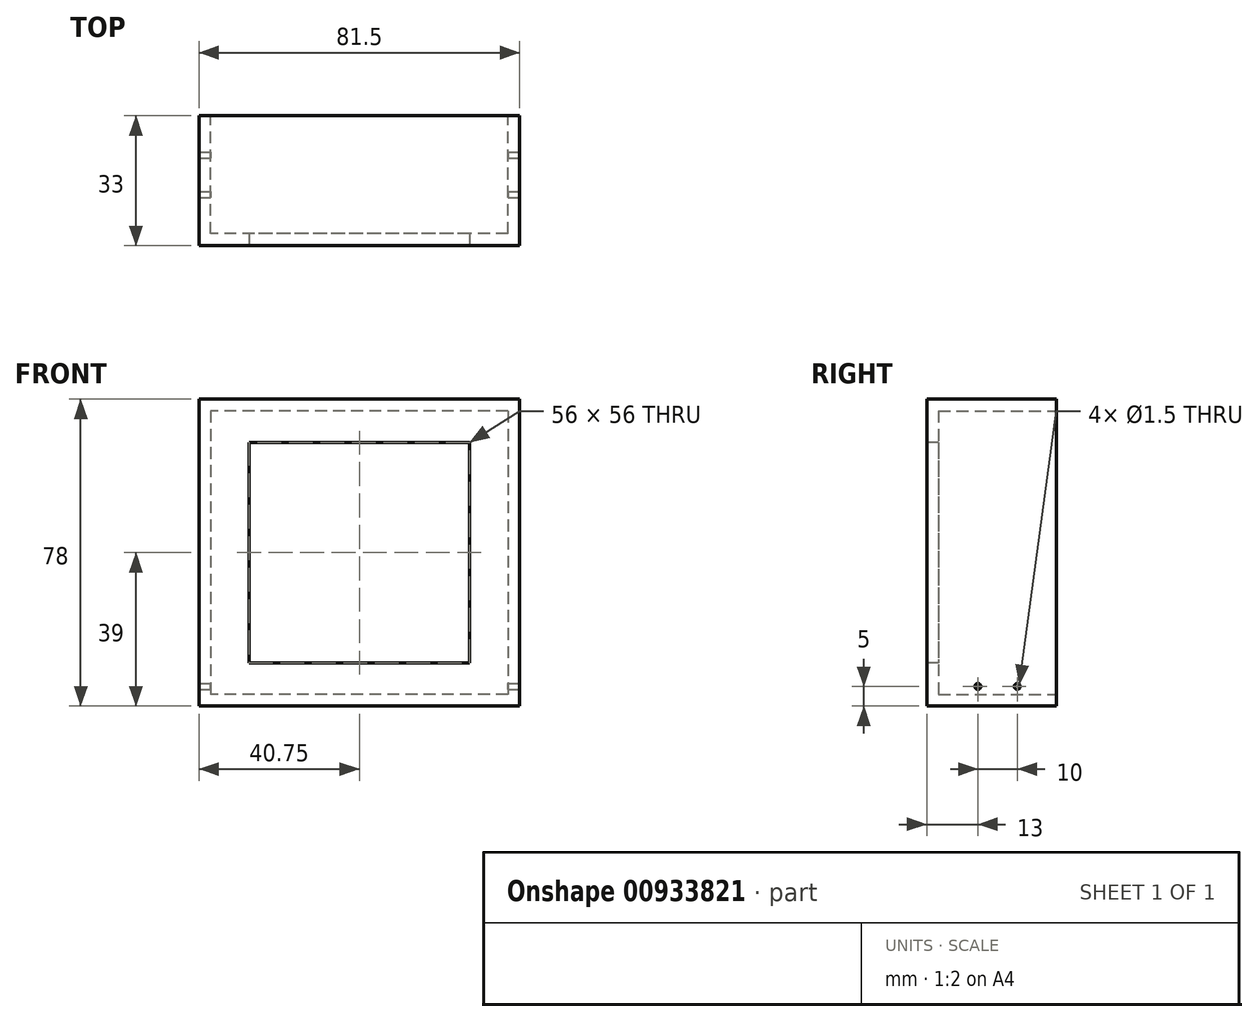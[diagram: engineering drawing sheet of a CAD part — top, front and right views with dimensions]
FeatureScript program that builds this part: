
annotation { "Feature Type Name" : "Feature", "Feature Type Description" : "" }
export const myFeature = defineFeature(function(context is Context, id is Id, definition is map)
    precondition{}
    {
        {
            var Q0;
            Q0=qCreatedBy(makeId("Front.planeOp"),FACE);
            var sketch = newSketch(context, id + "F0", { "sketchPlane" : qUnion([Q0])});
            skLineSegment(sketch, "E0.bottom", {"start": v(37.75, 36) * mm, "end": v(-37.75, 36) * mm});
            skLineSegment(sketch, "E0.top", {"start": v(37.75, -36) * mm, "end": v(-37.75, -36) * mm});
            skLineSegment(sketch, "E0.left", {"start": v(37.75, 36) * mm, "end": v(37.75, -36) * mm});
            skLineSegment(sketch, "E0.right", {"start": v(-37.75, 36) * mm, "end": v(-37.75, -36) * mm});
            skPoint(sketch, "E0.middle", {"position": v(0, 0) * mm});
            skLineSegment(sketch, "E1.bottom", {"start": v(40.75, 39) * mm, "end": v(-40.75, 39) * mm});
            skLineSegment(sketch, "E1.top", {"start": v(40.75, -39) * mm, "end": v(-40.75, -39) * mm});
            skLineSegment(sketch, "E1.left", {"start": v(40.75, 39) * mm, "end": v(40.75, -39) * mm});
            skLineSegment(sketch, "E1.right", {"start": v(-40.75, 39) * mm, "end": v(-40.75, -39) * mm});
            skSolve(sketch);
        }
        {
            var Q0;
            Q0 = qSketchRegion(id + "F0", true);
            extrude(context, id + "F1", {"entities" : qUnion([Q0]), "depth" : 33 * mm, "offsetDistance" : 25 * mm});
        }
        {
            var Q0;
            Q0=makeQuery(id+"F1.opExtrude","CAP_FACE",FACE,{"disambiguationData":[OSD([sQuery(id+"F0.wireOp",EDGE,"E0.bottom"),sQuery(id+"F0.wireOp",EDGE,"E0.top"),sQuery(id+"F0.wireOp",EDGE,"E0.left"),sQuery(id+"F0.wireOp",EDGE,"E0.right"),sQuery(id+"F0.wireOp",EDGE,"E1.bottom"),sQuery(id+"F0.wireOp",EDGE,"E1.top"),sQuery(id+"F0.wireOp",EDGE,"E1.left"),sQuery(id+"F0.wireOp",EDGE,"E1.right")])],"isStart":false});
            var sketch = newSketch(context, id + "F2", { "sketchPlane" : qUnion([Q0])});
            skLineSegment(sketch, "E2.bottom", {"start": v(-40.75, 39) * mm, "end": v(40.75, 39) * mm});
            skLineSegment(sketch, "E2.top", {"start": v(-40.75, -39) * mm, "end": v(40.75, -39) * mm});
            skLineSegment(sketch, "E2.left", {"start": v(-40.75, 39) * mm, "end": v(-40.75, -39) * mm});
            skLineSegment(sketch, "E2.right", {"start": v(40.75, 39) * mm, "end": v(40.75, -39) * mm});
            skLineSegment(sketch, "E3.bottom", {"start": v(28, 28) * mm, "end": v(-28, 28) * mm});
            skLineSegment(sketch, "E3.top", {"start": v(28, -28) * mm, "end": v(-28, -28) * mm});
            skLineSegment(sketch, "E3.left", {"start": v(28, 28) * mm, "end": v(28, -28) * mm});
            skLineSegment(sketch, "E3.right", {"start": v(-28, 28) * mm, "end": v(-28, -28) * mm});
            skPoint(sketch, "E3.middle", {"position": v(0, 0) * mm});
            skSolve(sketch);
        }
        {
            var Q0;
            Q0 = qSketchRegion(id + "F2", true);
            extrude(context, id + "F3", {"entities" : qUnion([Q0]), "operationType" : NewBodyOperationType.ADD, "oppositeDirection" : true, "depth" : 3 * mm, "offsetDistance" : 25 * mm});
        }
        {
            var Q0;
            Q0=makeQuery(id+"F1.opExtrude","SWEPT_FACE",FACE,{"disambiguationData":[OSD([sQuery(id+"F0.wireOp",EDGE,"E1.left")])]});
            var sketch = newSketch(context, id + "F4", { "sketchPlane" : qUnion([Q0])});
            skCircle(sketch, "E4", {"center": v(-10, -34) * mm, "radius": 0.75 * mm});
            skCircle(sketch, "E5", {"center": v(-20, -34) * mm, "radius": 0.75 * mm});
            skSolve(sketch);
        }
        {
            var Q0;
            Q0 = qSketchRegion(id + "F4", true);
            extrude(context, id + "F5", {"entities" : qUnion([Q0]), "operationType" : NewBodyOperationType.REMOVE, "oppositeDirection" : true, "depth" : 111.5 * mm, "offsetDistance" : 25 * mm});
        }
    });
